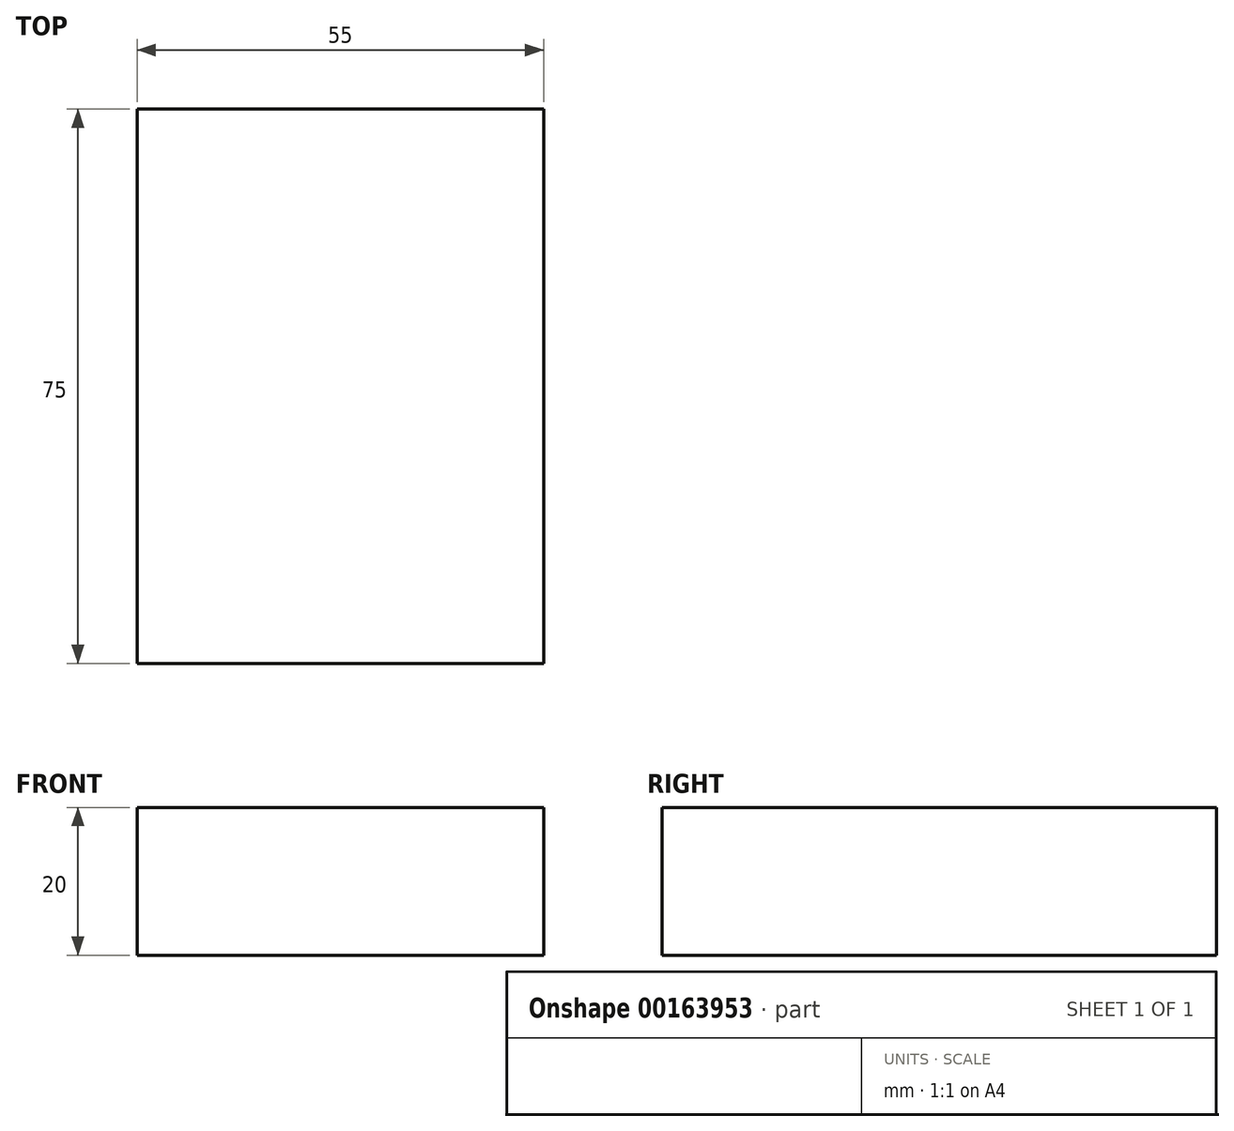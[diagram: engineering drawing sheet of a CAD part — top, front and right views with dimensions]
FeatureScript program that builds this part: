
annotation { "Feature Type Name" : "Feature", "Feature Type Description" : "" }
export const myFeature = defineFeature(function(context is Context, id is Id, definition is map)
    precondition{}
    {
        {
            var Q0;
            Q0=qCreatedBy(makeId("Top.planeOp"),FACE);
            var sketch = newSketch(context, id + "F0", { "sketchPlane" : qUnion([Q0])});
            skLineSegment(sketch, "E0.bottom", {"start": v(0, 0) * mm, "end": v(55, 0) * mm});
            skLineSegment(sketch, "E0.top", {"start": v(0, 75) * mm, "end": v(55, 75) * mm});
            skLineSegment(sketch, "E0.left", {"start": v(0, 0) * mm, "end": v(0, 75) * mm});
            skLineSegment(sketch, "E0.right", {"start": v(55, 0) * mm, "end": v(55, 75) * mm});
            skSolve(sketch);
        }
        {
            var Q0;
            Q0=makeQuery(id+"F0.imprint","IMPRINT",FACE,{"disambiguationData":[TD([[makeQuery(id+"F0.imprint","IMPRINT",EDGE,{"derivedFrom":sQuery(id+"F0.wireOp",EDGE,"E0.bottom")}),1.0]])]});
            extrude(context, id + "F1", {"entities" : qUnion([Q0]), "depth" : 20 * mm});
        }
    });
